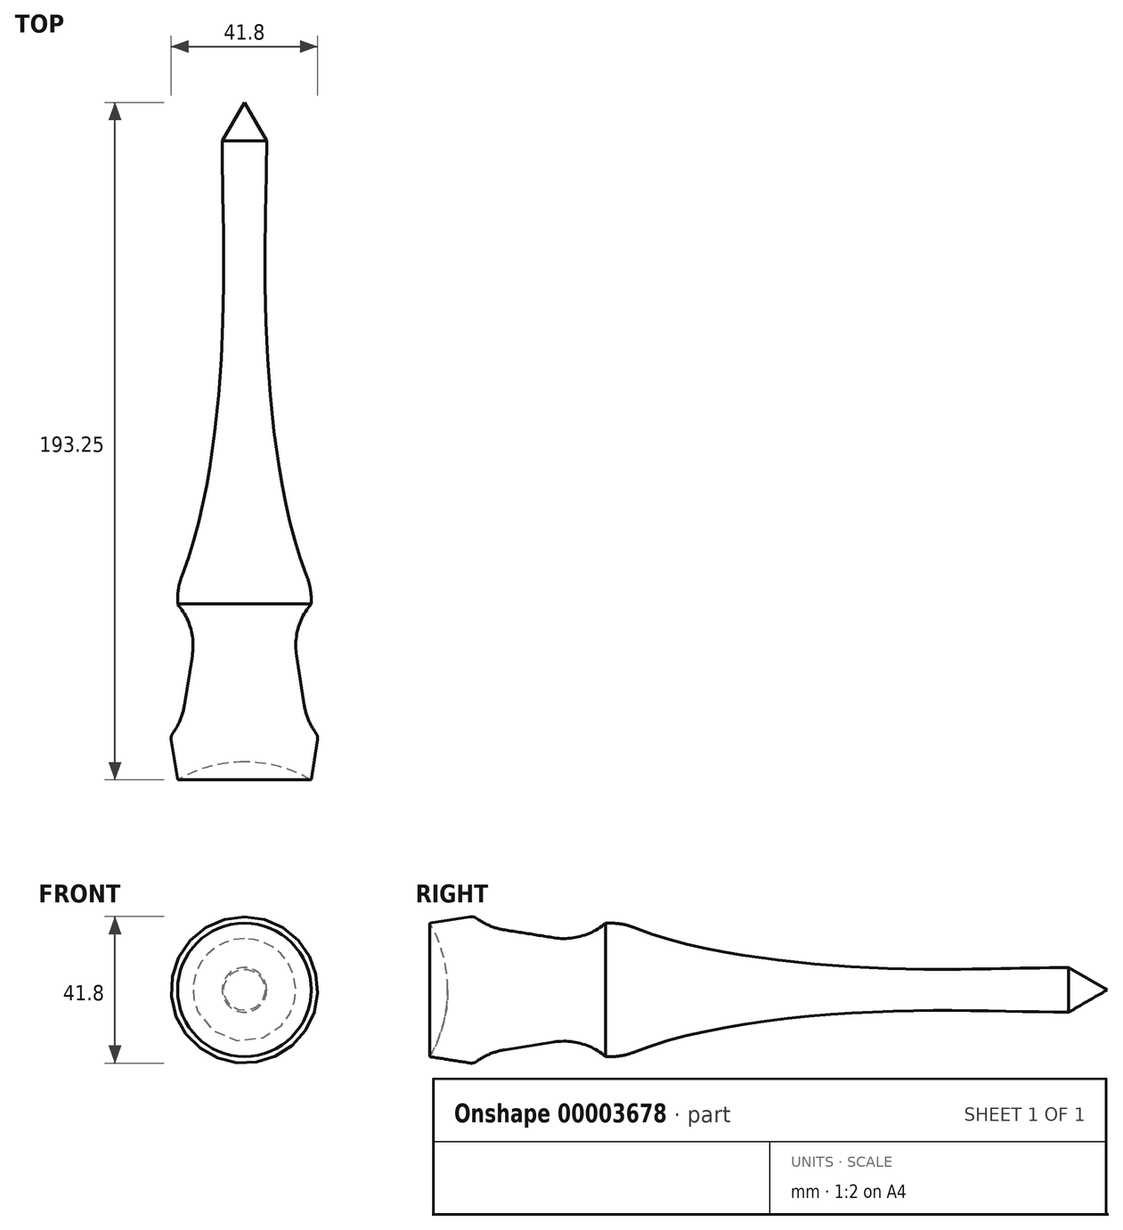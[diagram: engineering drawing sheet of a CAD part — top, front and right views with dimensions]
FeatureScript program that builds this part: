
annotation { "Feature Type Name" : "Feature", "Feature Type Description" : "" }
export const myFeature = defineFeature(function(context is Context, id is Id, definition is map)
    precondition{}
    {
        {
            var Q0;
            Q0=qCreatedBy(makeId("Right.planeOp"),FACE);
            var sketch = newSketch(context, id + "F0", { "sketchPlane" : qUnion([Q0])});
            skFitSpline(sketch, "E0", {"points": [v(50.8, 6.35) * mm, v(-6.35, 6.35) * mm, v(-76.2, 19.05) * mm], "startDerivative": vector(-96.31, 0) * mm, "endDerivative": vector(-97.57, 44.3) * mm});
            skLineSegment(sketch, "E1", {"start": v(-126.35, 0) * mm, "end": v(93.74, 0) * mm});
            skLineSegment(sketch, "E2", {"start": v(-76.2, 19.05) * mm, "end": v(-81.28, 19.05) * mm});
            skLineSegment(sketch, "E3", {"start": v(-81.28, 19.05) * mm, "end": v(-81.28, 12.54) * mm});
            skLineSegment(sketch, "E4", {"start": v(-81.28, 12.54) * mm, "end": v(-118.91, 18.5) * mm});
            skLineSegment(sketch, "E5", {"start": v(-118.91, 18.5) * mm, "end": v(-118.91, 21.04) * mm});
            skLineSegment(sketch, "E6", {"start": v(-118.91, 21.04) * mm, "end": v(-131.45, 19.05) * mm});
            skArc(sketch, "E7", {"start": v(-126.35, 0) * mm, "mid": v(-127.65, 9.86) * mm, "end": v(-131.45, 19.05) * mm});
            skLineSegment(sketch, "E8", {"start": v(50.8, 6.35) * mm, "end": v(61.8, 0) * mm});
            skSolve(sketch);
        }
        {
            var Q0;
            Q0=makeQuery(id+"F0.imprint","IMPRINT",FACE,{"disambiguationData":[TD([[makeQuery(id+"F0.imprint","IMPRINT",EDGE,{"derivedFrom":sQuery(id+"F0.wireOp",EDGE,"E0")}),1.0]])]});
            var Q1;
            Q1=sQuery(id+"F0.wireOp",EDGE,"E1");
            revolve(context, id + "F1", {"entities" : qUnion([Q0]), "axis" : qUnion([Q1]), "revolveType" : RevolveType.FULL});
        }
        {
            var Q0;
            Q0=makeQuery(id+"F1.opRevolve","SWEPT_EDGE",EDGE,{"disambiguationData":[OSD([sQuery(id+"F0.wireOp",EDGE,"E4"),sQuery(id+"F0.wireOp",EDGE,"E5")])]});
            var Q1;
            Q1=makeQuery(id+"F1.opRevolve","SWEPT_EDGE",EDGE,{"disambiguationData":[OSD([sQuery(id+"F0.wireOp",EDGE,"E0"),sQuery(id+"F0.wireOp",EDGE,"E2")])]});
            var Q2;
            Q2=makeQuery(id+"F1.opRevolve","SWEPT_EDGE",EDGE,{"disambiguationData":[OSD([sQuery(id+"F0.wireOp",EDGE,"E3"),sQuery(id+"F0.wireOp",EDGE,"E4")])]});
            fillet(context, id + "F2", {"entities" : qUnion([Q0, Q1, Q2]), "radius" : 18.29 * mm, "tangentPropagation" : true, "allowEdgeOverflow" : false});
        }
        {
            var Q0;
            Q0=makeQuery(id+"F2.opFillet","BLEND_EDGE",EDGE,{"blendedFrom":[makeQuery(id+"F1.opRevolve","SWEPT_EDGE",EDGE,{"disambiguationData":[OSD([sQuery(id+"F0.wireOp",EDGE,"E4"),sQuery(id+"F0.wireOp",EDGE,"E5")])]}),makeQuery(id+"F1.opRevolve","SWEPT_FACE",FACE,{"disambiguationData":[OSD([sQuery(id+"F0.wireOp",EDGE,"E6")])]})],"blendedInto":[makeQuery(id+"F1.opRevolve","SWEPT_FACE",FACE,{"disambiguationData":[OSD([sQuery(id+"F0.wireOp",EDGE,"E6")])]})]});
            fillet(context, id + "F3", {"entities" : qUnion([Q0]), "radius" : 2.54 * mm, "tangentPropagation" : true, "allowEdgeOverflow" : false});
        }
    });
